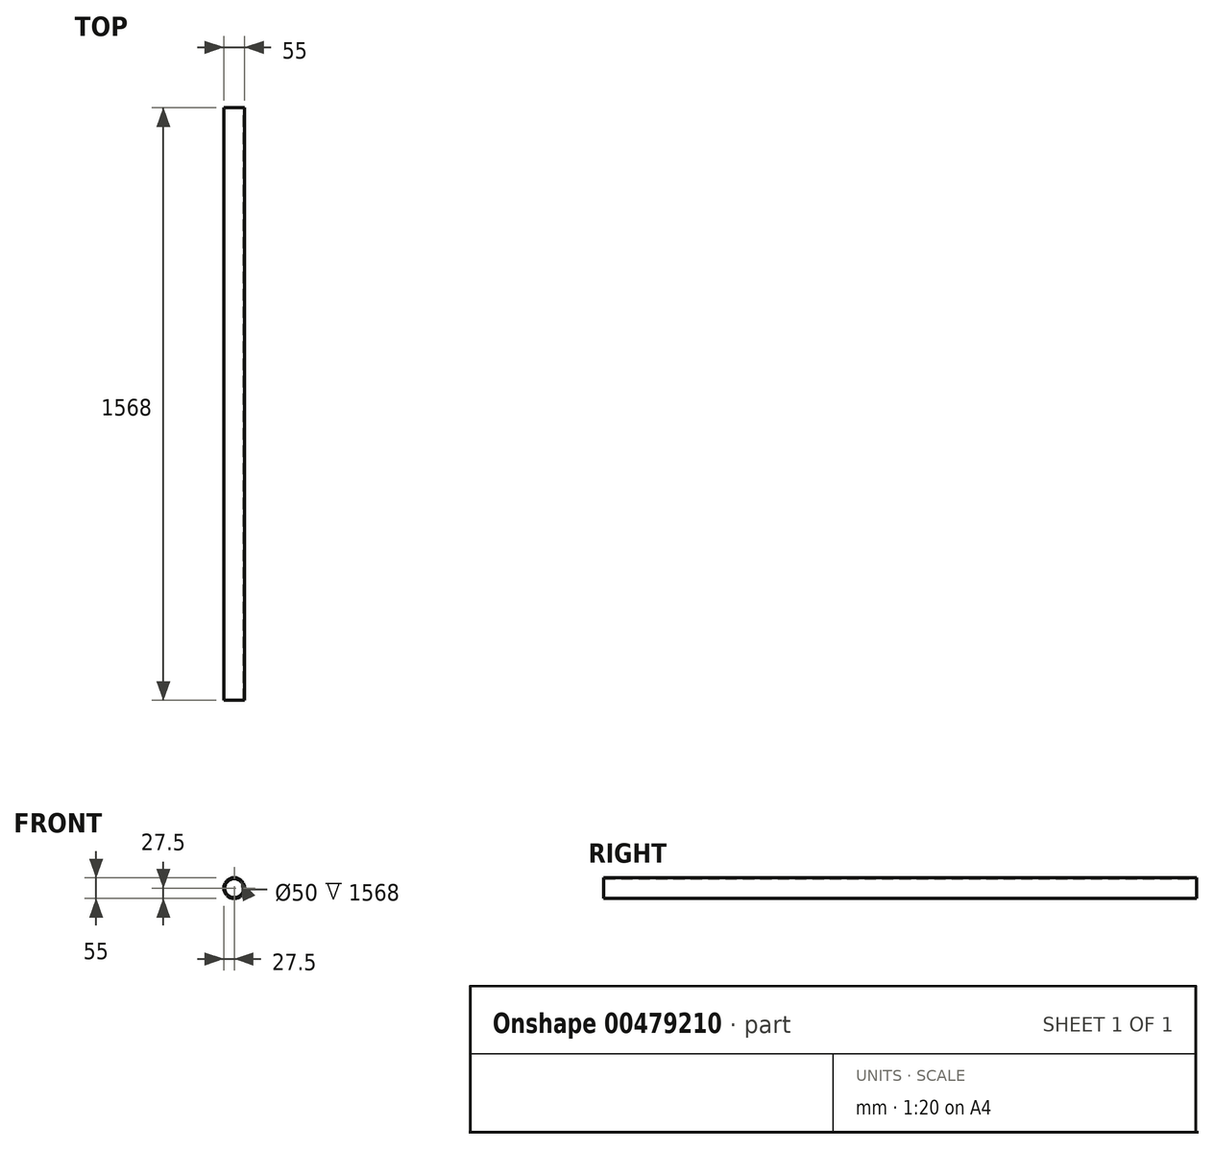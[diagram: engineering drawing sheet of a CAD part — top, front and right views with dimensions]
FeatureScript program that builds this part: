
annotation { "Feature Type Name" : "Feature", "Feature Type Description" : "" }
export const myFeature = defineFeature(function(context is Context, id is Id, definition is map)
    precondition{}
    {
        {
            var Q0;
            Q0=qCreatedBy(makeId("Front.planeOp"),FACE);
            var sketch = newSketch(context, id + "F0", { "sketchPlane" : qUnion([Q0])});
            skCircle(sketch, "E0", {"center": v(0, 0) * mm, "radius": 27.5 * mm});
            skCircle(sketch, "E1", {"center": v(0, 0) * mm, "radius": 25 * mm});
            skSolve(sketch);
        }
        {
            var Q0;
            Q0 = qSketchRegion(id + "F0", true);
            extrude(context, id + "F1", {"entities" : qUnion([Q0]), "depth" : 1568 * mm, "offsetDistance" : 25 * mm});
        }
    });
